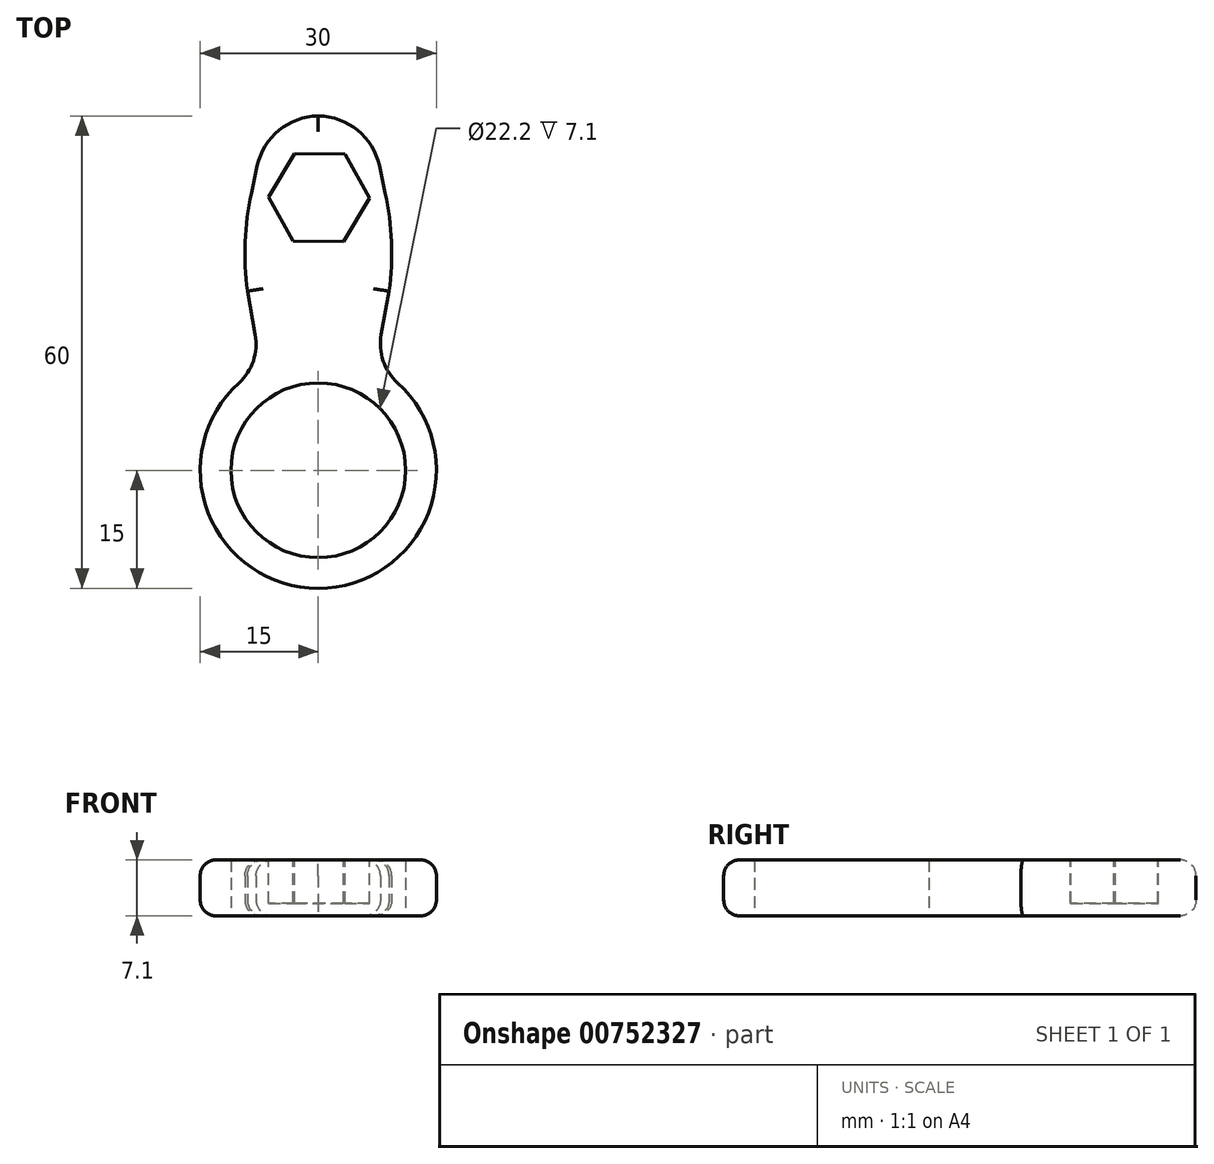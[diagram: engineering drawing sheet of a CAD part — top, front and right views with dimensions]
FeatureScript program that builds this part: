
annotation { "Feature Type Name" : "Feature", "Feature Type Description" : "" }
export const myFeature = defineFeature(function(context is Context, id is Id, definition is map)
    precondition{}
    {
        {
            var Q0;
            Q0=qCreatedBy(makeId("Top.planeOp"),FACE);
            var sketch = newSketch(context, id + "F0", { "sketchPlane" : qUnion([Q0])});
            skCircle(sketch, "E0", {"center": v(0, 0) * mm, "radius": 11.1 * mm});
            skCircle(sketch, "E1", {"center": v(0, 0) * mm, "radius": 15 * mm});
            skSolve(sketch);
        }
        {
            var Q0;
            Q0 = qSketchRegion(id + "F0", true);
            extrude(context, id + "F1", {"entities" : qUnion([Q0]), "depth" : 7.1 * mm, "offsetDistance" : 25 * mm});
        }
        {
            var Q0;
            Q0=qCreatedBy(makeId("Top.planeOp"),FACE);
            var sketch = newSketch(context, id + "F2", { "sketchPlane" : qUnion([Q0])});
            skLineSegment(sketch, "E2", {"start": v(-7, 42.2) * mm, "end": v(-8.5, 35.23) * mm});
            skLineSegment(sketch, "E3", {"start": v(-9, 22.75) * mm, "end": v(-8, 17.23) * mm});
            skArc(sketch, "E4", {"start": v(-8.5, 35.23) * mm, "mid": v(-9.29, 29.01) * mm, "end": v(-9, 22.75) * mm});
            skCircle(sketch, "E5", {"center": v(0, 0) * mm, "radius": 15 * mm});
            skArc(sketch, "E6", {"start": v(-10.08, 11.1) * mm, "mid": v(-8.25, 13.9) * mm, "end": v(-8, 17.23) * mm});
            skArc(sketch, "E7", {"start": v(0, 45) * mm, "mid": v(-3.76, 44.26) * mm, "end": v(-7, 42.2) * mm});
            skArc(sketch, "E8.MirrorCS", {"start": v(0, 45) * mm, "mid": v(3.76, 44.26) * mm, "end": v(7, 42.2) * mm});
            skArc(sketch, "E9.MirrorCS", {"start": v(8.5, 35.23) * mm, "mid": v(9.29, 29.01) * mm, "end": v(9, 22.75) * mm});
            skLineSegment(sketch, "E10.MirrorCS", {"start": v(9, 22.75) * mm, "end": v(8, 17.23) * mm});
            skLineSegment(sketch, "E11.MirrorCS", {"start": v(7, 42.2) * mm, "end": v(8.5, 35.23) * mm});
            skArc(sketch, "E12", {"start": v(8, 17.23) * mm, "mid": v(8.25, 13.9) * mm, "end": v(10.08, 11.1) * mm});
            skPoint(sketch, "E13.orphan", {"position": v(-10, 28.27) * mm});
            skPoint(sketch, "E14.orphan", {"position": v(10, 28.27) * mm});
            skArc(sketch, "E15.1.0", {"start": v(-38.97, -22.5) * mm, "mid": v(-40.2, -18.87) * mm, "end": v(-40.04, -15.03) * mm});
            skArc(sketch, "E15.1.1", {"start": v(-38.97, -22.5) * mm, "mid": v(-36.44, -25.39) * mm, "end": v(-33.04, -27.16) * mm});
            skLineSegment(sketch, "E15.1.2", {"start": v(-40.04, -15.03) * mm, "end": v(-34.76, -10.26) * mm});
            skArc(sketch, "E15.1.3", {"start": v(-4.58, -14.28) * mm, "mid": v(-7.91, -14.1) * mm, "end": v(-10.92, -15.54) * mm});
            skArc(sketch, "E15.1.4", {"start": v(-18.92, -1.69) * mm, "mid": v(-16.16, 0.2) * mm, "end": v(-14.66, 3.17) * mm});
            skPoint(sketch, "E15.1.5", {"position": v(-29.49, -5.48) * mm});
            skPoint(sketch, "E15.1.6", {"position": v(-19.49, -22.8) * mm});
            skLineSegment(sketch, "E15.1.7", {"start": v(-33.04, -27.16) * mm, "end": v(-26.26, -24.98) * mm});
            skArc(sketch, "E15.1.8", {"start": v(-34.76, -10.26) * mm, "mid": v(-29.77, -6.46) * mm, "end": v(-24.2, -3.58) * mm});
            skArc(sketch, "E15.1.9", {"start": v(-26.26, -24.98) * mm, "mid": v(-20.48, -22.55) * mm, "end": v(-15.2, -19.17) * mm});
            skLineSegment(sketch, "E15.1.10", {"start": v(-24.2, -3.58) * mm, "end": v(-18.92, -1.69) * mm});
            skLineSegment(sketch, "E15.1.11", {"start": v(-15.2, -19.17) * mm, "end": v(-10.92, -15.54) * mm});
            skArc(sketch, "E15.2.0", {"start": v(38.97, -22.5) * mm, "mid": v(36.44, -25.39) * mm, "end": v(33.04, -27.16) * mm});
            skArc(sketch, "E15.2.1", {"start": v(38.97, -22.5) * mm, "mid": v(40.2, -18.87) * mm, "end": v(40.04, -15.03) * mm});
            skLineSegment(sketch, "E15.2.2", {"start": v(33.04, -27.16) * mm, "end": v(26.26, -24.98) * mm});
            skArc(sketch, "E15.2.3", {"start": v(14.66, 3.17) * mm, "mid": v(16.16, 0.2) * mm, "end": v(18.92, -1.69) * mm});
            skArc(sketch, "E15.2.4", {"start": v(10.92, -15.54) * mm, "mid": v(7.91, -14.1) * mm, "end": v(4.58, -14.28) * mm});
            skPoint(sketch, "E15.2.5", {"position": v(19.49, -22.8) * mm});
            skPoint(sketch, "E15.2.6", {"position": v(29.49, -5.48) * mm});
            skLineSegment(sketch, "E15.2.7", {"start": v(40.04, -15.03) * mm, "end": v(34.76, -10.26) * mm});
            skArc(sketch, "E15.2.8", {"start": v(26.26, -24.98) * mm, "mid": v(20.48, -22.55) * mm, "end": v(15.2, -19.17) * mm});
            skArc(sketch, "E15.2.9", {"start": v(34.76, -10.26) * mm, "mid": v(29.77, -6.46) * mm, "end": v(24.2, -3.58) * mm});
            skLineSegment(sketch, "E15.2.10", {"start": v(15.2, -19.17) * mm, "end": v(10.92, -15.54) * mm});
            skLineSegment(sketch, "E15.2.11", {"start": v(24.2, -3.58) * mm, "end": v(18.92, -1.69) * mm});
            skCircle(sketch, "E16", {"center": v(0, 0) * mm, "radius": 4 * mm});
            skSolve(sketch);
        }
        {
            var Q0;
            Q0=makeQuery(id+"F2.imprint","IMPRINT",FACE,{"disambiguationData":[TD([[makeQuery(id+"F2.imprint","IMPRINT",EDGE,{"derivedFrom":sQuery(id+"F2.wireOp",EDGE,"E15.1.0")}),-1.0]])]});
            var Q1;
            Q1=makeQuery(id+"F2.imprint","IMPRINT",FACE,{"disambiguationData":[TD([[makeQuery(id+"F2.imprint","IMPRINT",EDGE,{"derivedFrom":sQuery(id+"F2.wireOp",EDGE,"E2")}),1.0]])]});
            var Q2;
            Q2=makeQuery(id+"F2.imprint","IMPRINT",FACE,{"disambiguationData":[TD([[makeQuery(id+"F2.imprint","IMPRINT",EDGE,{"derivedFrom":sQuery(id+"F2.wireOp",EDGE,"E15.2.0")}),-1.0]])]});
            extrude(context, id + "F3", {"entities" : qUnion([Q0, Q1, Q2]), "operationType" : NewBodyOperationType.ADD, "depth" : 7.1 * mm, "offsetDistance" : 25 * mm});
        }
        {
            var Q0;
            Q0=makeQuery(id+"F3.opExtrude","SWEPT_EDGE",EDGE,{"disambiguationData":[OSD([sQuery(id+"F2.wireOp",EDGE,"E8.MirrorCS"),sQuery(id+"F2.wireOp",EDGE,"E11.MirrorCS")])]});
            var Q1;
            Q1=makeQuery(id+"F3.opExtrude","SWEPT_EDGE",EDGE,{"disambiguationData":[OSD([sQuery(id+"F2.wireOp",EDGE,"E2"),sQuery(id+"F2.wireOp",EDGE,"E7")])]});
            var Q2;
            Q2=makeQuery(id+"F3.opExtrude","SWEPT_EDGE",EDGE,{"disambiguationData":[OSD([sQuery(id+"F2.wireOp",EDGE,"E15.2.1"),sQuery(id+"F2.wireOp",EDGE,"E15.2.7")])]});
            var Q3;
            Q3=makeQuery(id+"F3.opExtrude","SWEPT_EDGE",EDGE,{"disambiguationData":[OSD([sQuery(id+"F2.wireOp",EDGE,"E15.2.0"),sQuery(id+"F2.wireOp",EDGE,"E15.2.2")])]});
            var Q4;
            Q4=makeQuery(id+"F3.opExtrude","SWEPT_EDGE",EDGE,{"disambiguationData":[OSD([sQuery(id+"F2.wireOp",EDGE,"E15.1.1"),sQuery(id+"F2.wireOp",EDGE,"E15.1.7")])]});
            var Q5;
            Q5=makeQuery(id+"F3.opExtrude","SWEPT_EDGE",EDGE,{"disambiguationData":[OSD([sQuery(id+"F2.wireOp",EDGE,"E15.1.0"),sQuery(id+"F2.wireOp",EDGE,"E15.1.2")])]});
            fillet(context, id + "F4", {"entities" : qUnion([Q0, Q1, Q2, Q3, Q4, Q5]), "radius" : 8 * mm, "tangentPropagation" : true, "allowEdgeOverflow" : false});
        }
        {
            var Q0;
            {var subQ0=sQuery(id+"F2.wireOp",EDGE,"E5");Q0=makeQuery(id+"F3.boolean.opBoolean","MERGE",FACE,{"derivedFrom":[makeQuery(id+"F1.opExtrude","CAP_FACE",FACE,{"disambiguationData":[OSD([sQuery(id+"F0.wireOp",EDGE,"E0"),sQuery(id+"F0.wireOp",EDGE,"E1")])],"isStart":false}),makeQuery(id+"F3.opExtrude","CAP_FACE",FACE,{"disambiguationData":[OSD([sQuery(id+"F2.wireOp",EDGE,"E2"),sQuery(id+"F2.wireOp",EDGE,"E3"),sQuery(id+"F2.wireOp",EDGE,"E4"),subQ0,sQuery(id+"F2.wireOp",EDGE,"E6"),sQuery(id+"F2.wireOp",EDGE,"E7"),sQuery(id+"F2.wireOp",EDGE,"E8.MirrorCS"),sQuery(id+"F2.wireOp",EDGE,"E9.MirrorCS"),sQuery(id+"F2.wireOp",EDGE,"E10.MirrorCS"),sQuery(id+"F2.wireOp",EDGE,"E11.MirrorCS"),sQuery(id+"F2.wireOp",EDGE,"E12")])],"isStart":false}),makeQuery(id+"F3.opExtrude","CAP_FACE",FACE,{"disambiguationData":[OSD([subQ0,sQuery(id+"F2.wireOp",EDGE,"E15.1.0"),sQuery(id+"F2.wireOp",EDGE,"E15.1.1"),sQuery(id+"F2.wireOp",EDGE,"E15.1.2"),sQuery(id+"F2.wireOp",EDGE,"E15.1.3"),sQuery(id+"F2.wireOp",EDGE,"E15.1.4"),sQuery(id+"F2.wireOp",EDGE,"E15.1.7"),sQuery(id+"F2.wireOp",EDGE,"E15.1.8"),sQuery(id+"F2.wireOp",EDGE,"E15.1.9"),sQuery(id+"F2.wireOp",EDGE,"E15.1.10"),sQuery(id+"F2.wireOp",EDGE,"E15.1.11")])],"isStart":false}),makeQuery(id+"F3.opExtrude","CAP_FACE",FACE,{"disambiguationData":[OSD([subQ0,sQuery(id+"F2.wireOp",EDGE,"E15.2.0"),sQuery(id+"F2.wireOp",EDGE,"E15.2.1"),sQuery(id+"F2.wireOp",EDGE,"E15.2.2"),sQuery(id+"F2.wireOp",EDGE,"E15.2.3"),sQuery(id+"F2.wireOp",EDGE,"E15.2.4"),sQuery(id+"F2.wireOp",EDGE,"E15.2.7"),sQuery(id+"F2.wireOp",EDGE,"E15.2.8"),sQuery(id+"F2.wireOp",EDGE,"E15.2.9"),sQuery(id+"F2.wireOp",EDGE,"E15.2.10"),sQuery(id+"F2.wireOp",EDGE,"E15.2.11")])],"isStart":false})]});}
            var sketch = newSketch(context, id + "F5", { "sketchPlane" : qUnion([Q0])});
            skLineSegment(sketch, "E17", {"start": v(0, 0) * mm, "end": v(0.03, 45) * mm});
            skLineSegment(sketch, "E18", {"start": v(0, 0) * mm, "end": v(-38.96, -22.53) * mm});
            skLineSegment(sketch, "E19", {"start": v(0, 0) * mm, "end": v(38.99, -22.47) * mm});
            skCircle(sketch, "E20.cCircle", {"center": v(0.1, 34.64) * mm, "radius": 5.55 * mm, "construction": true});
            skLineSegment(sketch, "E20.0", {"start": v(3.22, 29.05) * mm, "end": v(-3.18, 29.13) * mm});
            skLineSegment(sketch, "E20.1", {"start": v(-3.18, 29.13) * mm, "end": v(-6.32, 34.73) * mm});
            skLineSegment(sketch, "E20.2", {"start": v(-6.32, 34.73) * mm, "end": v(-3.04, 40.23) * mm});
            skLineSegment(sketch, "E20.3", {"start": v(-3.04, 40.23) * mm, "end": v(3.37, 40.15) * mm});
            skLineSegment(sketch, "E20.4", {"start": v(3.37, 40.15) * mm, "end": v(6.5, 34.56) * mm});
            skLineSegment(sketch, "E20.5", {"start": v(6.5, 34.56) * mm, "end": v(3.22, 29.05) * mm});
            skPoint(sketch, "E20.0.midPoint", {"position": v(0.02, 29.1) * mm});
            skCircle(sketch, "E21.cCircle", {"center": v(29.95, -17.4) * mm, "radius": 5.55 * mm, "construction": true});
            skLineSegment(sketch, "E21.0", {"start": v(23.55, -17.27) * mm, "end": v(26.86, -11.79) * mm});
            skLineSegment(sketch, "E21.1", {"start": v(26.86, -11.79) * mm, "end": v(33.27, -11.92) * mm});
            skLineSegment(sketch, "E21.2", {"start": v(33.27, -11.92) * mm, "end": v(36.36, -17.53) * mm});
            skLineSegment(sketch, "E21.3", {"start": v(36.36, -17.53) * mm, "end": v(33.04, -23.01) * mm});
            skLineSegment(sketch, "E21.4", {"start": v(33.04, -23.01) * mm, "end": v(26.64, -22.88) * mm});
            skLineSegment(sketch, "E21.5", {"start": v(26.64, -22.88) * mm, "end": v(23.55, -17.27) * mm});
            skPoint(sketch, "E21.0.midPoint", {"position": v(25.2, -14.53) * mm});
            skCircle(sketch, "E22.cCircle", {"center": v(-29.95, -17.4) * mm, "radius": 5.55 * mm, "construction": true});
            skLineSegment(sketch, "E22.0", {"start": v(-26.86, -11.79) * mm, "end": v(-23.55, -17.27) * mm});
            skLineSegment(sketch, "E22.1", {"start": v(-23.55, -17.27) * mm, "end": v(-26.64, -22.88) * mm});
            skLineSegment(sketch, "E22.2", {"start": v(-26.64, -22.88) * mm, "end": v(-33.04, -23.01) * mm});
            skLineSegment(sketch, "E22.3", {"start": v(-33.04, -23.01) * mm, "end": v(-36.36, -17.53) * mm});
            skLineSegment(sketch, "E22.4", {"start": v(-36.36, -17.53) * mm, "end": v(-33.27, -11.92) * mm});
            skLineSegment(sketch, "E22.5", {"start": v(-33.27, -11.92) * mm, "end": v(-26.86, -11.79) * mm});
            skPoint(sketch, "E22.0.midPoint", {"position": v(-25.2, -14.53) * mm});
            skSolve(sketch);
        }
        {
            var Q0;
            Q0 = qSketchRegion(id + "F5", true);
            extrude(context, id + "F6", {"entities" : qUnion([Q0]), "operationType" : NewBodyOperationType.REMOVE, "oppositeDirection" : true, "depth" : 5.5 * mm, "offsetDistance" : 25 * mm});
        }
        {
            var Q0;
            {var subQ1=sQuery(id+"F2.wireOp",EDGE,"E12");var subQ2=sQuery(id+"F0.wireOp",EDGE,"E1");Q0=makeQuery(id+"F3.boolean.opBoolean","SPLIT",EDGE,{"disambiguationData":[TD([makeQuery(id+"F3.opExtrude","SWEPT_FACE",FACE,{"disambiguationData":[OSD([subQ1])]})])],"derivedFrom":makeQuery(id+"F1.opExtrude","CAP_EDGE",EDGE,{"disambiguationData":[OSD([subQ2])],"isStart":false})});}
            var Q1;
            {var subQ2=sQuery(id+"F2.wireOp",EDGE,"E6");var subQ3=sQuery(id+"F0.wireOp",EDGE,"E1");Q1=makeQuery(id+"F3.boolean.opBoolean","SPLIT",EDGE,{"disambiguationData":[TD([makeQuery(id+"F3.opExtrude","SWEPT_FACE",FACE,{"disambiguationData":[OSD([subQ2])]})])],"derivedFrom":makeQuery(id+"F1.opExtrude","CAP_EDGE",EDGE,{"disambiguationData":[OSD([subQ3])],"isStart":false})});}
            var Q2;
            {var subQ0=sQuery(id+"F2.wireOp",EDGE,"E15.1.3");var subQ2=sQuery(id+"F0.wireOp",EDGE,"E1");Q2=makeQuery(id+"F3.boolean.opBoolean","SPLIT",EDGE,{"disambiguationData":[TD([makeQuery(id+"F3.opExtrude","SWEPT_FACE",FACE,{"disambiguationData":[OSD([subQ0])]})])],"derivedFrom":makeQuery(id+"F1.opExtrude","CAP_EDGE",EDGE,{"disambiguationData":[OSD([subQ2])],"isStart":false})});}
            var Q3;
            {var subQ0=sQuery(id+"F2.wireOp",EDGE,"E15.2.2");var subQ1=sQuery(id+"F2.wireOp",EDGE,"E15.2.0");var subQ2=sQuery(id+"F2.wireOp",EDGE,"E5");Q3=makeQuery(id+"F4.opFillet","BLEND_EDGE",EDGE,{"blendedFrom":[makeQuery(id+"F3.opExtrude","SWEPT_EDGE",EDGE,{"disambiguationData":[OSD([subQ1,subQ0])]}),makeQuery(id+"F3.boolean.opBoolean","MERGE",FACE,{"derivedFrom":[makeQuery(id+"F1.opExtrude","CAP_FACE",FACE,{"disambiguationData":[OSD([sQuery(id+"F0.wireOp",EDGE,"E0"),sQuery(id+"F0.wireOp",EDGE,"E1")])],"isStart":false}),makeQuery(id+"F3.opExtrude","CAP_FACE",FACE,{"disambiguationData":[OSD([sQuery(id+"F2.wireOp",EDGE,"E2"),sQuery(id+"F2.wireOp",EDGE,"E3"),sQuery(id+"F2.wireOp",EDGE,"E4"),subQ2,sQuery(id+"F2.wireOp",EDGE,"E6"),sQuery(id+"F2.wireOp",EDGE,"E7"),sQuery(id+"F2.wireOp",EDGE,"E8.MirrorCS"),sQuery(id+"F2.wireOp",EDGE,"E9.MirrorCS"),sQuery(id+"F2.wireOp",EDGE,"E10.MirrorCS"),sQuery(id+"F2.wireOp",EDGE,"E11.MirrorCS"),sQuery(id+"F2.wireOp",EDGE,"E12")])],"isStart":false}),makeQuery(id+"F3.opExtrude","CAP_FACE",FACE,{"disambiguationData":[OSD([subQ2,sQuery(id+"F2.wireOp",EDGE,"E15.1.0"),sQuery(id+"F2.wireOp",EDGE,"E15.1.1"),sQuery(id+"F2.wireOp",EDGE,"E15.1.2"),sQuery(id+"F2.wireOp",EDGE,"E15.1.3"),sQuery(id+"F2.wireOp",EDGE,"E15.1.4"),sQuery(id+"F2.wireOp",EDGE,"E15.1.7"),sQuery(id+"F2.wireOp",EDGE,"E15.1.8"),sQuery(id+"F2.wireOp",EDGE,"E15.1.9"),sQuery(id+"F2.wireOp",EDGE,"E15.1.10"),sQuery(id+"F2.wireOp",EDGE,"E15.1.11")])],"isStart":false}),makeQuery(id+"F3.opExtrude","CAP_FACE",FACE,{"disambiguationData":[OSD([subQ2,subQ1,sQuery(id+"F2.wireOp",EDGE,"E15.2.1"),subQ0,sQuery(id+"F2.wireOp",EDGE,"E15.2.3"),sQuery(id+"F2.wireOp",EDGE,"E15.2.4"),sQuery(id+"F2.wireOp",EDGE,"E15.2.7"),sQuery(id+"F2.wireOp",EDGE,"E15.2.8"),sQuery(id+"F2.wireOp",EDGE,"E15.2.9"),sQuery(id+"F2.wireOp",EDGE,"E15.2.10"),sQuery(id+"F2.wireOp",EDGE,"E15.2.11")])],"isStart":false})]})],"blendedInto":[makeQuery(id+"F3.boolean.opBoolean","MERGE",FACE,{"derivedFrom":[makeQuery(id+"F1.opExtrude","CAP_FACE",FACE,{"disambiguationData":[OSD([sQuery(id+"F0.wireOp",EDGE,"E0"),sQuery(id+"F0.wireOp",EDGE,"E1")])],"isStart":false}),makeQuery(id+"F3.opExtrude","CAP_FACE",FACE,{"disambiguationData":[OSD([sQuery(id+"F2.wireOp",EDGE,"E2"),sQuery(id+"F2.wireOp",EDGE,"E3"),sQuery(id+"F2.wireOp",EDGE,"E4"),subQ2,sQuery(id+"F2.wireOp",EDGE,"E6"),sQuery(id+"F2.wireOp",EDGE,"E7"),sQuery(id+"F2.wireOp",EDGE,"E8.MirrorCS"),sQuery(id+"F2.wireOp",EDGE,"E9.MirrorCS"),sQuery(id+"F2.wireOp",EDGE,"E10.MirrorCS"),sQuery(id+"F2.wireOp",EDGE,"E11.MirrorCS"),sQuery(id+"F2.wireOp",EDGE,"E12")])],"isStart":false}),makeQuery(id+"F3.opExtrude","CAP_FACE",FACE,{"disambiguationData":[OSD([subQ2,sQuery(id+"F2.wireOp",EDGE,"E15.1.0"),sQuery(id+"F2.wireOp",EDGE,"E15.1.1"),sQuery(id+"F2.wireOp",EDGE,"E15.1.2"),sQuery(id+"F2.wireOp",EDGE,"E15.1.3"),sQuery(id+"F2.wireOp",EDGE,"E15.1.4"),sQuery(id+"F2.wireOp",EDGE,"E15.1.7"),sQuery(id+"F2.wireOp",EDGE,"E15.1.8"),sQuery(id+"F2.wireOp",EDGE,"E15.1.9"),sQuery(id+"F2.wireOp",EDGE,"E15.1.10"),sQuery(id+"F2.wireOp",EDGE,"E15.1.11")])],"isStart":false}),makeQuery(id+"F3.opExtrude","CAP_FACE",FACE,{"disambiguationData":[OSD([subQ2,subQ1,sQuery(id+"F2.wireOp",EDGE,"E15.2.1"),subQ0,sQuery(id+"F2.wireOp",EDGE,"E15.2.3"),sQuery(id+"F2.wireOp",EDGE,"E15.2.4"),sQuery(id+"F2.wireOp",EDGE,"E15.2.7"),sQuery(id+"F2.wireOp",EDGE,"E15.2.8"),sQuery(id+"F2.wireOp",EDGE,"E15.2.9"),sQuery(id+"F2.wireOp",EDGE,"E15.2.10"),sQuery(id+"F2.wireOp",EDGE,"E15.2.11")])],"isStart":false})]})]});}
            var Q4;
            Q4=makeQuery(id+"F3.opExtrude","CAP_EDGE",EDGE,{"disambiguationData":[OSD([sQuery(id+"F2.wireOp",EDGE,"E15.2.7")])],"isStart":false});
            var Q5;
            {var subQ0=sQuery(id+"F2.wireOp",EDGE,"E5");var subQ1=sQuery(id+"F2.wireOp",EDGE,"E15.1.7");var subQ2=sQuery(id+"F2.wireOp",EDGE,"E15.1.1");Q5=makeQuery(id+"F4.opFillet","BLEND_EDGE",EDGE,{"blendedFrom":[makeQuery(id+"F3.opExtrude","SWEPT_EDGE",EDGE,{"disambiguationData":[OSD([subQ2,subQ1])]}),makeQuery(id+"F3.boolean.opBoolean","MERGE",FACE,{"derivedFrom":[makeQuery(id+"F1.opExtrude","CAP_FACE",FACE,{"disambiguationData":[OSD([sQuery(id+"F0.wireOp",EDGE,"E0"),sQuery(id+"F0.wireOp",EDGE,"E1")])],"isStart":false}),makeQuery(id+"F3.opExtrude","CAP_FACE",FACE,{"disambiguationData":[OSD([sQuery(id+"F2.wireOp",EDGE,"E2"),sQuery(id+"F2.wireOp",EDGE,"E3"),sQuery(id+"F2.wireOp",EDGE,"E4"),subQ0,sQuery(id+"F2.wireOp",EDGE,"E6"),sQuery(id+"F2.wireOp",EDGE,"E7"),sQuery(id+"F2.wireOp",EDGE,"E8.MirrorCS"),sQuery(id+"F2.wireOp",EDGE,"E9.MirrorCS"),sQuery(id+"F2.wireOp",EDGE,"E10.MirrorCS"),sQuery(id+"F2.wireOp",EDGE,"E11.MirrorCS"),sQuery(id+"F2.wireOp",EDGE,"E12")])],"isStart":false}),makeQuery(id+"F3.opExtrude","CAP_FACE",FACE,{"disambiguationData":[OSD([subQ0,sQuery(id+"F2.wireOp",EDGE,"E15.1.0"),subQ2,sQuery(id+"F2.wireOp",EDGE,"E15.1.2"),sQuery(id+"F2.wireOp",EDGE,"E15.1.3"),sQuery(id+"F2.wireOp",EDGE,"E15.1.4"),subQ1,sQuery(id+"F2.wireOp",EDGE,"E15.1.8"),sQuery(id+"F2.wireOp",EDGE,"E15.1.9"),sQuery(id+"F2.wireOp",EDGE,"E15.1.10"),sQuery(id+"F2.wireOp",EDGE,"E15.1.11")])],"isStart":false}),makeQuery(id+"F3.opExtrude","CAP_FACE",FACE,{"disambiguationData":[OSD([subQ0,sQuery(id+"F2.wireOp",EDGE,"E15.2.0"),sQuery(id+"F2.wireOp",EDGE,"E15.2.1"),sQuery(id+"F2.wireOp",EDGE,"E15.2.2"),sQuery(id+"F2.wireOp",EDGE,"E15.2.3"),sQuery(id+"F2.wireOp",EDGE,"E15.2.4"),sQuery(id+"F2.wireOp",EDGE,"E15.2.7"),sQuery(id+"F2.wireOp",EDGE,"E15.2.8"),sQuery(id+"F2.wireOp",EDGE,"E15.2.9"),sQuery(id+"F2.wireOp",EDGE,"E15.2.10"),sQuery(id+"F2.wireOp",EDGE,"E15.2.11")])],"isStart":false})]})],"blendedInto":[makeQuery(id+"F3.boolean.opBoolean","MERGE",FACE,{"derivedFrom":[makeQuery(id+"F1.opExtrude","CAP_FACE",FACE,{"disambiguationData":[OSD([sQuery(id+"F0.wireOp",EDGE,"E0"),sQuery(id+"F0.wireOp",EDGE,"E1")])],"isStart":false}),makeQuery(id+"F3.opExtrude","CAP_FACE",FACE,{"disambiguationData":[OSD([sQuery(id+"F2.wireOp",EDGE,"E2"),sQuery(id+"F2.wireOp",EDGE,"E3"),sQuery(id+"F2.wireOp",EDGE,"E4"),subQ0,sQuery(id+"F2.wireOp",EDGE,"E6"),sQuery(id+"F2.wireOp",EDGE,"E7"),sQuery(id+"F2.wireOp",EDGE,"E8.MirrorCS"),sQuery(id+"F2.wireOp",EDGE,"E9.MirrorCS"),sQuery(id+"F2.wireOp",EDGE,"E10.MirrorCS"),sQuery(id+"F2.wireOp",EDGE,"E11.MirrorCS"),sQuery(id+"F2.wireOp",EDGE,"E12")])],"isStart":false}),makeQuery(id+"F3.opExtrude","CAP_FACE",FACE,{"disambiguationData":[OSD([subQ0,sQuery(id+"F2.wireOp",EDGE,"E15.1.0"),subQ2,sQuery(id+"F2.wireOp",EDGE,"E15.1.2"),sQuery(id+"F2.wireOp",EDGE,"E15.1.3"),sQuery(id+"F2.wireOp",EDGE,"E15.1.4"),subQ1,sQuery(id+"F2.wireOp",EDGE,"E15.1.8"),sQuery(id+"F2.wireOp",EDGE,"E15.1.9"),sQuery(id+"F2.wireOp",EDGE,"E15.1.10"),sQuery(id+"F2.wireOp",EDGE,"E15.1.11")])],"isStart":false}),makeQuery(id+"F3.opExtrude","CAP_FACE",FACE,{"disambiguationData":[OSD([subQ0,sQuery(id+"F2.wireOp",EDGE,"E15.2.0"),sQuery(id+"F2.wireOp",EDGE,"E15.2.1"),sQuery(id+"F2.wireOp",EDGE,"E15.2.2"),sQuery(id+"F2.wireOp",EDGE,"E15.2.3"),sQuery(id+"F2.wireOp",EDGE,"E15.2.4"),sQuery(id+"F2.wireOp",EDGE,"E15.2.7"),sQuery(id+"F2.wireOp",EDGE,"E15.2.8"),sQuery(id+"F2.wireOp",EDGE,"E15.2.9"),sQuery(id+"F2.wireOp",EDGE,"E15.2.10"),sQuery(id+"F2.wireOp",EDGE,"E15.2.11")])],"isStart":false})]})]});}
            var Q6;
            Q6=makeQuery(id+"F3.opExtrude","CAP_EDGE",EDGE,{"disambiguationData":[OSD([sQuery(id+"F2.wireOp",EDGE,"E15.1.2")])],"isStart":false});
            var Q7;
            {var subQ0=sQuery(id+"F2.wireOp",EDGE,"E5");var subQ1=sQuery(id+"F2.wireOp",EDGE,"E11.MirrorCS");var subQ2=sQuery(id+"F2.wireOp",EDGE,"E8.MirrorCS");Q7=makeQuery(id+"F4.opFillet","BLEND_EDGE",EDGE,{"blendedFrom":[makeQuery(id+"F3.opExtrude","SWEPT_EDGE",EDGE,{"disambiguationData":[OSD([subQ2,subQ1])]}),makeQuery(id+"F3.boolean.opBoolean","MERGE",FACE,{"derivedFrom":[makeQuery(id+"F1.opExtrude","CAP_FACE",FACE,{"disambiguationData":[OSD([sQuery(id+"F0.wireOp",EDGE,"E0"),sQuery(id+"F0.wireOp",EDGE,"E1")])],"isStart":false}),makeQuery(id+"F3.opExtrude","CAP_FACE",FACE,{"disambiguationData":[OSD([sQuery(id+"F2.wireOp",EDGE,"E2"),sQuery(id+"F2.wireOp",EDGE,"E3"),sQuery(id+"F2.wireOp",EDGE,"E4"),subQ0,sQuery(id+"F2.wireOp",EDGE,"E6"),sQuery(id+"F2.wireOp",EDGE,"E7"),subQ2,sQuery(id+"F2.wireOp",EDGE,"E9.MirrorCS"),sQuery(id+"F2.wireOp",EDGE,"E10.MirrorCS"),subQ1,sQuery(id+"F2.wireOp",EDGE,"E12")])],"isStart":false}),makeQuery(id+"F3.opExtrude","CAP_FACE",FACE,{"disambiguationData":[OSD([subQ0,sQuery(id+"F2.wireOp",EDGE,"E15.1.0"),sQuery(id+"F2.wireOp",EDGE,"E15.1.1"),sQuery(id+"F2.wireOp",EDGE,"E15.1.2"),sQuery(id+"F2.wireOp",EDGE,"E15.1.3"),sQuery(id+"F2.wireOp",EDGE,"E15.1.4"),sQuery(id+"F2.wireOp",EDGE,"E15.1.7"),sQuery(id+"F2.wireOp",EDGE,"E15.1.8"),sQuery(id+"F2.wireOp",EDGE,"E15.1.9"),sQuery(id+"F2.wireOp",EDGE,"E15.1.10"),sQuery(id+"F2.wireOp",EDGE,"E15.1.11")])],"isStart":false}),makeQuery(id+"F3.opExtrude","CAP_FACE",FACE,{"disambiguationData":[OSD([subQ0,sQuery(id+"F2.wireOp",EDGE,"E15.2.0"),sQuery(id+"F2.wireOp",EDGE,"E15.2.1"),sQuery(id+"F2.wireOp",EDGE,"E15.2.2"),sQuery(id+"F2.wireOp",EDGE,"E15.2.3"),sQuery(id+"F2.wireOp",EDGE,"E15.2.4"),sQuery(id+"F2.wireOp",EDGE,"E15.2.7"),sQuery(id+"F2.wireOp",EDGE,"E15.2.8"),sQuery(id+"F2.wireOp",EDGE,"E15.2.9"),sQuery(id+"F2.wireOp",EDGE,"E15.2.10"),sQuery(id+"F2.wireOp",EDGE,"E15.2.11")])],"isStart":false})]})],"blendedInto":[makeQuery(id+"F3.boolean.opBoolean","MERGE",FACE,{"derivedFrom":[makeQuery(id+"F1.opExtrude","CAP_FACE",FACE,{"disambiguationData":[OSD([sQuery(id+"F0.wireOp",EDGE,"E0"),sQuery(id+"F0.wireOp",EDGE,"E1")])],"isStart":false}),makeQuery(id+"F3.opExtrude","CAP_FACE",FACE,{"disambiguationData":[OSD([sQuery(id+"F2.wireOp",EDGE,"E2"),sQuery(id+"F2.wireOp",EDGE,"E3"),sQuery(id+"F2.wireOp",EDGE,"E4"),subQ0,sQuery(id+"F2.wireOp",EDGE,"E6"),sQuery(id+"F2.wireOp",EDGE,"E7"),subQ2,sQuery(id+"F2.wireOp",EDGE,"E9.MirrorCS"),sQuery(id+"F2.wireOp",EDGE,"E10.MirrorCS"),subQ1,sQuery(id+"F2.wireOp",EDGE,"E12")])],"isStart":false}),makeQuery(id+"F3.opExtrude","CAP_FACE",FACE,{"disambiguationData":[OSD([subQ0,sQuery(id+"F2.wireOp",EDGE,"E15.1.0"),sQuery(id+"F2.wireOp",EDGE,"E15.1.1"),sQuery(id+"F2.wireOp",EDGE,"E15.1.2"),sQuery(id+"F2.wireOp",EDGE,"E15.1.3"),sQuery(id+"F2.wireOp",EDGE,"E15.1.4"),sQuery(id+"F2.wireOp",EDGE,"E15.1.7"),sQuery(id+"F2.wireOp",EDGE,"E15.1.8"),sQuery(id+"F2.wireOp",EDGE,"E15.1.9"),sQuery(id+"F2.wireOp",EDGE,"E15.1.10"),sQuery(id+"F2.wireOp",EDGE,"E15.1.11")])],"isStart":false}),makeQuery(id+"F3.opExtrude","CAP_FACE",FACE,{"disambiguationData":[OSD([subQ0,sQuery(id+"F2.wireOp",EDGE,"E15.2.0"),sQuery(id+"F2.wireOp",EDGE,"E15.2.1"),sQuery(id+"F2.wireOp",EDGE,"E15.2.2"),sQuery(id+"F2.wireOp",EDGE,"E15.2.3"),sQuery(id+"F2.wireOp",EDGE,"E15.2.4"),sQuery(id+"F2.wireOp",EDGE,"E15.2.7"),sQuery(id+"F2.wireOp",EDGE,"E15.2.8"),sQuery(id+"F2.wireOp",EDGE,"E15.2.9"),sQuery(id+"F2.wireOp",EDGE,"E15.2.10"),sQuery(id+"F2.wireOp",EDGE,"E15.2.11")])],"isStart":false})]})]});}
            var Q8;
            Q8=makeQuery(id+"F3.opExtrude","CAP_EDGE",EDGE,{"disambiguationData":[OSD([sQuery(id+"F2.wireOp",EDGE,"E2")])],"isStart":false});
            fillet(context, id + "F7", {"entities" : qUnion([Q0, Q1, Q2, Q3, Q4, Q5, Q6, Q7, Q8]), "radius" : 2 * mm, "tangentPropagation" : true, "allowEdgeOverflow" : false});
        }
        {
            var Q0;
            {var subQ2=sQuery(id+"F2.wireOp",EDGE,"E6");var subQ3=sQuery(id+"F0.wireOp",EDGE,"E1");Q0=makeQuery(id+"F3.boolean.opBoolean","SPLIT",EDGE,{"disambiguationData":[TD([makeQuery(id+"F3.opExtrude","SWEPT_FACE",FACE,{"disambiguationData":[OSD([subQ2])]})])],"derivedFrom":makeQuery(id+"F1.opExtrude","CAP_EDGE",EDGE,{"disambiguationData":[OSD([subQ3])],"isStart":true})});}
            var Q1;
            {var subQ1=sQuery(id+"F2.wireOp",EDGE,"E12");var subQ2=sQuery(id+"F0.wireOp",EDGE,"E1");Q1=makeQuery(id+"F3.boolean.opBoolean","SPLIT",EDGE,{"disambiguationData":[TD([makeQuery(id+"F3.opExtrude","SWEPT_FACE",FACE,{"disambiguationData":[OSD([subQ1])]})])],"derivedFrom":makeQuery(id+"F1.opExtrude","CAP_EDGE",EDGE,{"disambiguationData":[OSD([subQ2])],"isStart":true})});}
            var Q2;
            {var subQ0=sQuery(id+"F2.wireOp",EDGE,"E15.1.3");var subQ2=sQuery(id+"F0.wireOp",EDGE,"E1");Q2=makeQuery(id+"F3.boolean.opBoolean","SPLIT",EDGE,{"disambiguationData":[TD([makeQuery(id+"F3.opExtrude","SWEPT_FACE",FACE,{"disambiguationData":[OSD([subQ0])]})])],"derivedFrom":makeQuery(id+"F1.opExtrude","CAP_EDGE",EDGE,{"disambiguationData":[OSD([subQ2])],"isStart":true})});}
            var Q3;
            {var subQ0=sQuery(id+"F2.wireOp",EDGE,"E5");var subQ1=sQuery(id+"F2.wireOp",EDGE,"E15.1.2");var subQ2=sQuery(id+"F2.wireOp",EDGE,"E15.1.0");Q3=makeQuery(id+"F4.opFillet","BLEND_EDGE",EDGE,{"blendedFrom":[makeQuery(id+"F3.opExtrude","SWEPT_EDGE",EDGE,{"disambiguationData":[OSD([subQ2,subQ1])]}),makeQuery(id+"F3.boolean.opBoolean","MERGE",FACE,{"derivedFrom":[makeQuery(id+"F1.opExtrude","CAP_FACE",FACE,{"disambiguationData":[OSD([sQuery(id+"F0.wireOp",EDGE,"E0"),sQuery(id+"F0.wireOp",EDGE,"E1")])],"isStart":true}),makeQuery(id+"F3.opExtrude","CAP_FACE",FACE,{"disambiguationData":[OSD([sQuery(id+"F2.wireOp",EDGE,"E2"),sQuery(id+"F2.wireOp",EDGE,"E3"),sQuery(id+"F2.wireOp",EDGE,"E4"),subQ0,sQuery(id+"F2.wireOp",EDGE,"E6"),sQuery(id+"F2.wireOp",EDGE,"E7"),sQuery(id+"F2.wireOp",EDGE,"E8.MirrorCS"),sQuery(id+"F2.wireOp",EDGE,"E9.MirrorCS"),sQuery(id+"F2.wireOp",EDGE,"E10.MirrorCS"),sQuery(id+"F2.wireOp",EDGE,"E11.MirrorCS"),sQuery(id+"F2.wireOp",EDGE,"E12")])],"isStart":true}),makeQuery(id+"F3.opExtrude","CAP_FACE",FACE,{"disambiguationData":[OSD([subQ0,subQ2,sQuery(id+"F2.wireOp",EDGE,"E15.1.1"),subQ1,sQuery(id+"F2.wireOp",EDGE,"E15.1.3"),sQuery(id+"F2.wireOp",EDGE,"E15.1.4"),sQuery(id+"F2.wireOp",EDGE,"E15.1.7"),sQuery(id+"F2.wireOp",EDGE,"E15.1.8"),sQuery(id+"F2.wireOp",EDGE,"E15.1.9"),sQuery(id+"F2.wireOp",EDGE,"E15.1.10"),sQuery(id+"F2.wireOp",EDGE,"E15.1.11")])],"isStart":true}),makeQuery(id+"F3.opExtrude","CAP_FACE",FACE,{"disambiguationData":[OSD([subQ0,sQuery(id+"F2.wireOp",EDGE,"E15.2.0"),sQuery(id+"F2.wireOp",EDGE,"E15.2.1"),sQuery(id+"F2.wireOp",EDGE,"E15.2.2"),sQuery(id+"F2.wireOp",EDGE,"E15.2.3"),sQuery(id+"F2.wireOp",EDGE,"E15.2.4"),sQuery(id+"F2.wireOp",EDGE,"E15.2.7"),sQuery(id+"F2.wireOp",EDGE,"E15.2.8"),sQuery(id+"F2.wireOp",EDGE,"E15.2.9"),sQuery(id+"F2.wireOp",EDGE,"E15.2.10"),sQuery(id+"F2.wireOp",EDGE,"E15.2.11")])],"isStart":true})]})],"blendedInto":[makeQuery(id+"F3.boolean.opBoolean","MERGE",FACE,{"derivedFrom":[makeQuery(id+"F1.opExtrude","CAP_FACE",FACE,{"disambiguationData":[OSD([sQuery(id+"F0.wireOp",EDGE,"E0"),sQuery(id+"F0.wireOp",EDGE,"E1")])],"isStart":true}),makeQuery(id+"F3.opExtrude","CAP_FACE",FACE,{"disambiguationData":[OSD([sQuery(id+"F2.wireOp",EDGE,"E2"),sQuery(id+"F2.wireOp",EDGE,"E3"),sQuery(id+"F2.wireOp",EDGE,"E4"),subQ0,sQuery(id+"F2.wireOp",EDGE,"E6"),sQuery(id+"F2.wireOp",EDGE,"E7"),sQuery(id+"F2.wireOp",EDGE,"E8.MirrorCS"),sQuery(id+"F2.wireOp",EDGE,"E9.MirrorCS"),sQuery(id+"F2.wireOp",EDGE,"E10.MirrorCS"),sQuery(id+"F2.wireOp",EDGE,"E11.MirrorCS"),sQuery(id+"F2.wireOp",EDGE,"E12")])],"isStart":true}),makeQuery(id+"F3.opExtrude","CAP_FACE",FACE,{"disambiguationData":[OSD([subQ0,subQ2,sQuery(id+"F2.wireOp",EDGE,"E15.1.1"),subQ1,sQuery(id+"F2.wireOp",EDGE,"E15.1.3"),sQuery(id+"F2.wireOp",EDGE,"E15.1.4"),sQuery(id+"F2.wireOp",EDGE,"E15.1.7"),sQuery(id+"F2.wireOp",EDGE,"E15.1.8"),sQuery(id+"F2.wireOp",EDGE,"E15.1.9"),sQuery(id+"F2.wireOp",EDGE,"E15.1.10"),sQuery(id+"F2.wireOp",EDGE,"E15.1.11")])],"isStart":true}),makeQuery(id+"F3.opExtrude","CAP_FACE",FACE,{"disambiguationData":[OSD([subQ0,sQuery(id+"F2.wireOp",EDGE,"E15.2.0"),sQuery(id+"F2.wireOp",EDGE,"E15.2.1"),sQuery(id+"F2.wireOp",EDGE,"E15.2.2"),sQuery(id+"F2.wireOp",EDGE,"E15.2.3"),sQuery(id+"F2.wireOp",EDGE,"E15.2.4"),sQuery(id+"F2.wireOp",EDGE,"E15.2.7"),sQuery(id+"F2.wireOp",EDGE,"E15.2.8"),sQuery(id+"F2.wireOp",EDGE,"E15.2.9"),sQuery(id+"F2.wireOp",EDGE,"E15.2.10"),sQuery(id+"F2.wireOp",EDGE,"E15.2.11")])],"isStart":true})]})]});}
            var Q4;
            Q4=makeQuery(id+"F3.opExtrude","CAP_EDGE",EDGE,{"disambiguationData":[OSD([sQuery(id+"F2.wireOp",EDGE,"E15.1.7")])],"isStart":true});
            var Q5;
            {var subQ0=sQuery(id+"F2.wireOp",EDGE,"E5");var subQ1=sQuery(id+"F2.wireOp",EDGE,"E7");var subQ2=sQuery(id+"F2.wireOp",EDGE,"E2");Q5=makeQuery(id+"F4.opFillet","BLEND_EDGE",EDGE,{"blendedFrom":[makeQuery(id+"F3.opExtrude","SWEPT_EDGE",EDGE,{"disambiguationData":[OSD([subQ2,subQ1])]}),makeQuery(id+"F3.boolean.opBoolean","MERGE",FACE,{"derivedFrom":[makeQuery(id+"F1.opExtrude","CAP_FACE",FACE,{"disambiguationData":[OSD([sQuery(id+"F0.wireOp",EDGE,"E0"),sQuery(id+"F0.wireOp",EDGE,"E1")])],"isStart":true}),makeQuery(id+"F3.opExtrude","CAP_FACE",FACE,{"disambiguationData":[OSD([subQ2,sQuery(id+"F2.wireOp",EDGE,"E3"),sQuery(id+"F2.wireOp",EDGE,"E4"),subQ0,sQuery(id+"F2.wireOp",EDGE,"E6"),subQ1,sQuery(id+"F2.wireOp",EDGE,"E8.MirrorCS"),sQuery(id+"F2.wireOp",EDGE,"E9.MirrorCS"),sQuery(id+"F2.wireOp",EDGE,"E10.MirrorCS"),sQuery(id+"F2.wireOp",EDGE,"E11.MirrorCS"),sQuery(id+"F2.wireOp",EDGE,"E12")])],"isStart":true}),makeQuery(id+"F3.opExtrude","CAP_FACE",FACE,{"disambiguationData":[OSD([subQ0,sQuery(id+"F2.wireOp",EDGE,"E15.1.0"),sQuery(id+"F2.wireOp",EDGE,"E15.1.1"),sQuery(id+"F2.wireOp",EDGE,"E15.1.2"),sQuery(id+"F2.wireOp",EDGE,"E15.1.3"),sQuery(id+"F2.wireOp",EDGE,"E15.1.4"),sQuery(id+"F2.wireOp",EDGE,"E15.1.7"),sQuery(id+"F2.wireOp",EDGE,"E15.1.8"),sQuery(id+"F2.wireOp",EDGE,"E15.1.9"),sQuery(id+"F2.wireOp",EDGE,"E15.1.10"),sQuery(id+"F2.wireOp",EDGE,"E15.1.11")])],"isStart":true}),makeQuery(id+"F3.opExtrude","CAP_FACE",FACE,{"disambiguationData":[OSD([subQ0,sQuery(id+"F2.wireOp",EDGE,"E15.2.0"),sQuery(id+"F2.wireOp",EDGE,"E15.2.1"),sQuery(id+"F2.wireOp",EDGE,"E15.2.2"),sQuery(id+"F2.wireOp",EDGE,"E15.2.3"),sQuery(id+"F2.wireOp",EDGE,"E15.2.4"),sQuery(id+"F2.wireOp",EDGE,"E15.2.7"),sQuery(id+"F2.wireOp",EDGE,"E15.2.8"),sQuery(id+"F2.wireOp",EDGE,"E15.2.9"),sQuery(id+"F2.wireOp",EDGE,"E15.2.10"),sQuery(id+"F2.wireOp",EDGE,"E15.2.11")])],"isStart":true})]})],"blendedInto":[makeQuery(id+"F3.boolean.opBoolean","MERGE",FACE,{"derivedFrom":[makeQuery(id+"F1.opExtrude","CAP_FACE",FACE,{"disambiguationData":[OSD([sQuery(id+"F0.wireOp",EDGE,"E0"),sQuery(id+"F0.wireOp",EDGE,"E1")])],"isStart":true}),makeQuery(id+"F3.opExtrude","CAP_FACE",FACE,{"disambiguationData":[OSD([subQ2,sQuery(id+"F2.wireOp",EDGE,"E3"),sQuery(id+"F2.wireOp",EDGE,"E4"),subQ0,sQuery(id+"F2.wireOp",EDGE,"E6"),subQ1,sQuery(id+"F2.wireOp",EDGE,"E8.MirrorCS"),sQuery(id+"F2.wireOp",EDGE,"E9.MirrorCS"),sQuery(id+"F2.wireOp",EDGE,"E10.MirrorCS"),sQuery(id+"F2.wireOp",EDGE,"E11.MirrorCS"),sQuery(id+"F2.wireOp",EDGE,"E12")])],"isStart":true}),makeQuery(id+"F3.opExtrude","CAP_FACE",FACE,{"disambiguationData":[OSD([subQ0,sQuery(id+"F2.wireOp",EDGE,"E15.1.0"),sQuery(id+"F2.wireOp",EDGE,"E15.1.1"),sQuery(id+"F2.wireOp",EDGE,"E15.1.2"),sQuery(id+"F2.wireOp",EDGE,"E15.1.3"),sQuery(id+"F2.wireOp",EDGE,"E15.1.4"),sQuery(id+"F2.wireOp",EDGE,"E15.1.7"),sQuery(id+"F2.wireOp",EDGE,"E15.1.8"),sQuery(id+"F2.wireOp",EDGE,"E15.1.9"),sQuery(id+"F2.wireOp",EDGE,"E15.1.10"),sQuery(id+"F2.wireOp",EDGE,"E15.1.11")])],"isStart":true}),makeQuery(id+"F3.opExtrude","CAP_FACE",FACE,{"disambiguationData":[OSD([subQ0,sQuery(id+"F2.wireOp",EDGE,"E15.2.0"),sQuery(id+"F2.wireOp",EDGE,"E15.2.1"),sQuery(id+"F2.wireOp",EDGE,"E15.2.2"),sQuery(id+"F2.wireOp",EDGE,"E15.2.3"),sQuery(id+"F2.wireOp",EDGE,"E15.2.4"),sQuery(id+"F2.wireOp",EDGE,"E15.2.7"),sQuery(id+"F2.wireOp",EDGE,"E15.2.8"),sQuery(id+"F2.wireOp",EDGE,"E15.2.9"),sQuery(id+"F2.wireOp",EDGE,"E15.2.10"),sQuery(id+"F2.wireOp",EDGE,"E15.2.11")])],"isStart":true})]})]});}
            var Q6;
            Q6=makeQuery(id+"F3.opExtrude","CAP_EDGE",EDGE,{"disambiguationData":[OSD([sQuery(id+"F2.wireOp",EDGE,"E11.MirrorCS")])],"isStart":true});
            var Q7;
            {var subQ0=sQuery(id+"F2.wireOp",EDGE,"E15.2.7");var subQ1=sQuery(id+"F2.wireOp",EDGE,"E15.2.1");var subQ2=sQuery(id+"F2.wireOp",EDGE,"E5");Q7=makeQuery(id+"F4.opFillet","BLEND_EDGE",EDGE,{"blendedFrom":[makeQuery(id+"F3.opExtrude","SWEPT_EDGE",EDGE,{"disambiguationData":[OSD([subQ1,subQ0])]}),makeQuery(id+"F3.boolean.opBoolean","MERGE",FACE,{"derivedFrom":[makeQuery(id+"F1.opExtrude","CAP_FACE",FACE,{"disambiguationData":[OSD([sQuery(id+"F0.wireOp",EDGE,"E0"),sQuery(id+"F0.wireOp",EDGE,"E1")])],"isStart":true}),makeQuery(id+"F3.opExtrude","CAP_FACE",FACE,{"disambiguationData":[OSD([sQuery(id+"F2.wireOp",EDGE,"E2"),sQuery(id+"F2.wireOp",EDGE,"E3"),sQuery(id+"F2.wireOp",EDGE,"E4"),subQ2,sQuery(id+"F2.wireOp",EDGE,"E6"),sQuery(id+"F2.wireOp",EDGE,"E7"),sQuery(id+"F2.wireOp",EDGE,"E8.MirrorCS"),sQuery(id+"F2.wireOp",EDGE,"E9.MirrorCS"),sQuery(id+"F2.wireOp",EDGE,"E10.MirrorCS"),sQuery(id+"F2.wireOp",EDGE,"E11.MirrorCS"),sQuery(id+"F2.wireOp",EDGE,"E12")])],"isStart":true}),makeQuery(id+"F3.opExtrude","CAP_FACE",FACE,{"disambiguationData":[OSD([subQ2,sQuery(id+"F2.wireOp",EDGE,"E15.1.0"),sQuery(id+"F2.wireOp",EDGE,"E15.1.1"),sQuery(id+"F2.wireOp",EDGE,"E15.1.2"),sQuery(id+"F2.wireOp",EDGE,"E15.1.3"),sQuery(id+"F2.wireOp",EDGE,"E15.1.4"),sQuery(id+"F2.wireOp",EDGE,"E15.1.7"),sQuery(id+"F2.wireOp",EDGE,"E15.1.8"),sQuery(id+"F2.wireOp",EDGE,"E15.1.9"),sQuery(id+"F2.wireOp",EDGE,"E15.1.10"),sQuery(id+"F2.wireOp",EDGE,"E15.1.11")])],"isStart":true}),makeQuery(id+"F3.opExtrude","CAP_FACE",FACE,{"disambiguationData":[OSD([subQ2,sQuery(id+"F2.wireOp",EDGE,"E15.2.0"),subQ1,sQuery(id+"F2.wireOp",EDGE,"E15.2.2"),sQuery(id+"F2.wireOp",EDGE,"E15.2.3"),sQuery(id+"F2.wireOp",EDGE,"E15.2.4"),subQ0,sQuery(id+"F2.wireOp",EDGE,"E15.2.8"),sQuery(id+"F2.wireOp",EDGE,"E15.2.9"),sQuery(id+"F2.wireOp",EDGE,"E15.2.10"),sQuery(id+"F2.wireOp",EDGE,"E15.2.11")])],"isStart":true})]})],"blendedInto":[makeQuery(id+"F3.boolean.opBoolean","MERGE",FACE,{"derivedFrom":[makeQuery(id+"F1.opExtrude","CAP_FACE",FACE,{"disambiguationData":[OSD([sQuery(id+"F0.wireOp",EDGE,"E0"),sQuery(id+"F0.wireOp",EDGE,"E1")])],"isStart":true}),makeQuery(id+"F3.opExtrude","CAP_FACE",FACE,{"disambiguationData":[OSD([sQuery(id+"F2.wireOp",EDGE,"E2"),sQuery(id+"F2.wireOp",EDGE,"E3"),sQuery(id+"F2.wireOp",EDGE,"E4"),subQ2,sQuery(id+"F2.wireOp",EDGE,"E6"),sQuery(id+"F2.wireOp",EDGE,"E7"),sQuery(id+"F2.wireOp",EDGE,"E8.MirrorCS"),sQuery(id+"F2.wireOp",EDGE,"E9.MirrorCS"),sQuery(id+"F2.wireOp",EDGE,"E10.MirrorCS"),sQuery(id+"F2.wireOp",EDGE,"E11.MirrorCS"),sQuery(id+"F2.wireOp",EDGE,"E12")])],"isStart":true}),makeQuery(id+"F3.opExtrude","CAP_FACE",FACE,{"disambiguationData":[OSD([subQ2,sQuery(id+"F2.wireOp",EDGE,"E15.1.0"),sQuery(id+"F2.wireOp",EDGE,"E15.1.1"),sQuery(id+"F2.wireOp",EDGE,"E15.1.2"),sQuery(id+"F2.wireOp",EDGE,"E15.1.3"),sQuery(id+"F2.wireOp",EDGE,"E15.1.4"),sQuery(id+"F2.wireOp",EDGE,"E15.1.7"),sQuery(id+"F2.wireOp",EDGE,"E15.1.8"),sQuery(id+"F2.wireOp",EDGE,"E15.1.9"),sQuery(id+"F2.wireOp",EDGE,"E15.1.10"),sQuery(id+"F2.wireOp",EDGE,"E15.1.11")])],"isStart":true}),makeQuery(id+"F3.opExtrude","CAP_FACE",FACE,{"disambiguationData":[OSD([subQ2,sQuery(id+"F2.wireOp",EDGE,"E15.2.0"),subQ1,sQuery(id+"F2.wireOp",EDGE,"E15.2.2"),sQuery(id+"F2.wireOp",EDGE,"E15.2.3"),sQuery(id+"F2.wireOp",EDGE,"E15.2.4"),subQ0,sQuery(id+"F2.wireOp",EDGE,"E15.2.8"),sQuery(id+"F2.wireOp",EDGE,"E15.2.9"),sQuery(id+"F2.wireOp",EDGE,"E15.2.10"),sQuery(id+"F2.wireOp",EDGE,"E15.2.11")])],"isStart":true})]})]});}
            var Q8;
            Q8=makeQuery(id+"F3.opExtrude","CAP_EDGE",EDGE,{"disambiguationData":[OSD([sQuery(id+"F2.wireOp",EDGE,"E15.2.2")])],"isStart":true});
            fillet(context, id + "F8", {"entities" : qUnion([Q0, Q1, Q2, Q3, Q4, Q5, Q6, Q7, Q8]), "radius" : 2 * mm, "tangentPropagation" : true, "allowEdgeOverflow" : false});
        }
    });
